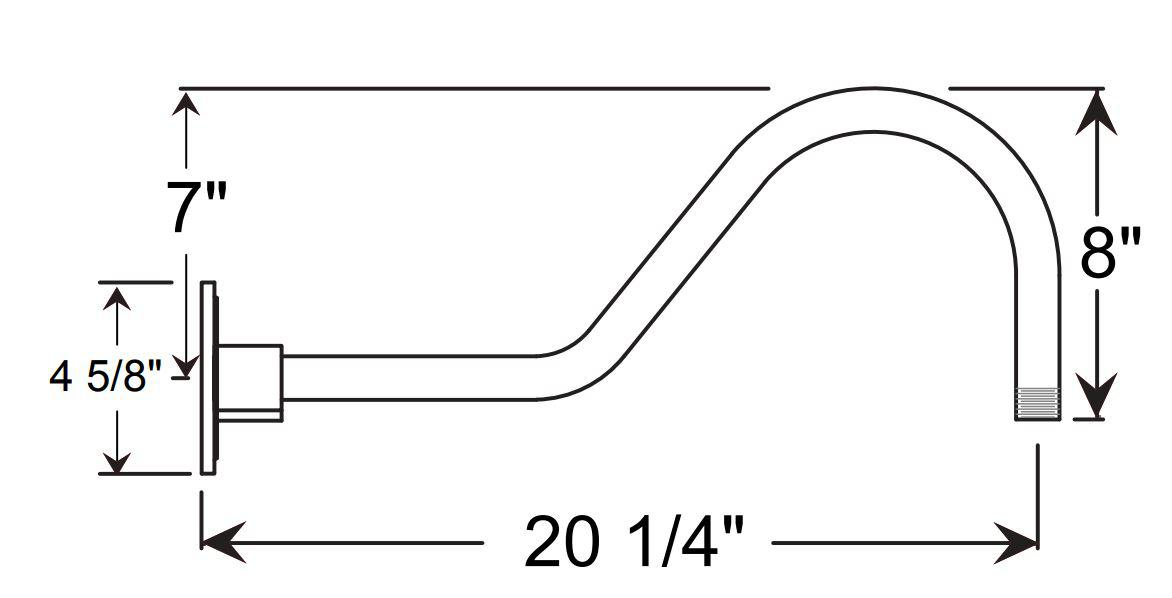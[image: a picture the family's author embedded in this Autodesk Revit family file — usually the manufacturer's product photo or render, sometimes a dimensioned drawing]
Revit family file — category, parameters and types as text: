
# Revit family: Warehouse Flat LED 20,24,27
name_source: partatom
category: Lighting Fixtures
units: mm (PartAtom-declared; Revit-internal decimal feet)

## family parameters
Always vertical = Yes
Cut with Voids When Loaded = No
Light Source = Yes
OmniClass Number = 23.80.70.00
OmniClass Title = Lighting
Part Type = Normal
Room Calculation Point = No
Round Connector Dimension = Use Diameter
Shared = No
Work Plane-Based = No

## types (3) — shared parameters
Apparent Load = 24 VA
BULB = Yes
Body Colour = Spun aluminium
Body Material = body
Bulb = Bulb
CRI = >90
Canopy Body = BLACK
Color Filter = 16777215
Construction Material = Heavy Duty spun aluminum.
Default Elevation = 0' - 0"
Description = 120-277 Voltage
Dimming = 1%
Dimming Lamp Color Temperature Shift = <None>
Efficiency = 65-125 lumens per watt
Lamp = LED
Life = L70 50,000 hours
Load Classification = Lighting
Manufacturer = ANP Lighting
Photometric Web File = generic
Power Factor = 1
Tilt Angle = 90.00°
URL = https://www.anplighting.com
Voltage = 120 V
Warranty = 5 year limited warranty
Wattage Comments = 24 W
b = 0' - 2"

## per-type parameters (varying)
| type | Fixture Diameter | Fixture Height | WF520 | WF524 | WF527 | Weight | a |
| WF520 | 1' - 8" | 0' - 6" | Yes | No | No | 2.5 lb | 0' - 6" |
| WF524 | 2' - 0" | 0' - 6 3/4" | No | Yes | No | 5.5 lb | 0' - 6 3/4" |
| WF527 | 2' - 3" | 0' - 7 3/4" | No | No | Yes | 6.5 lb | 0' - 7 3/4" |

note: column(s) folded — value = type name in every type: Model

## geometry (parser evidence)
native form markers: Sweep x30
no freeform markers — native parametric forms only
